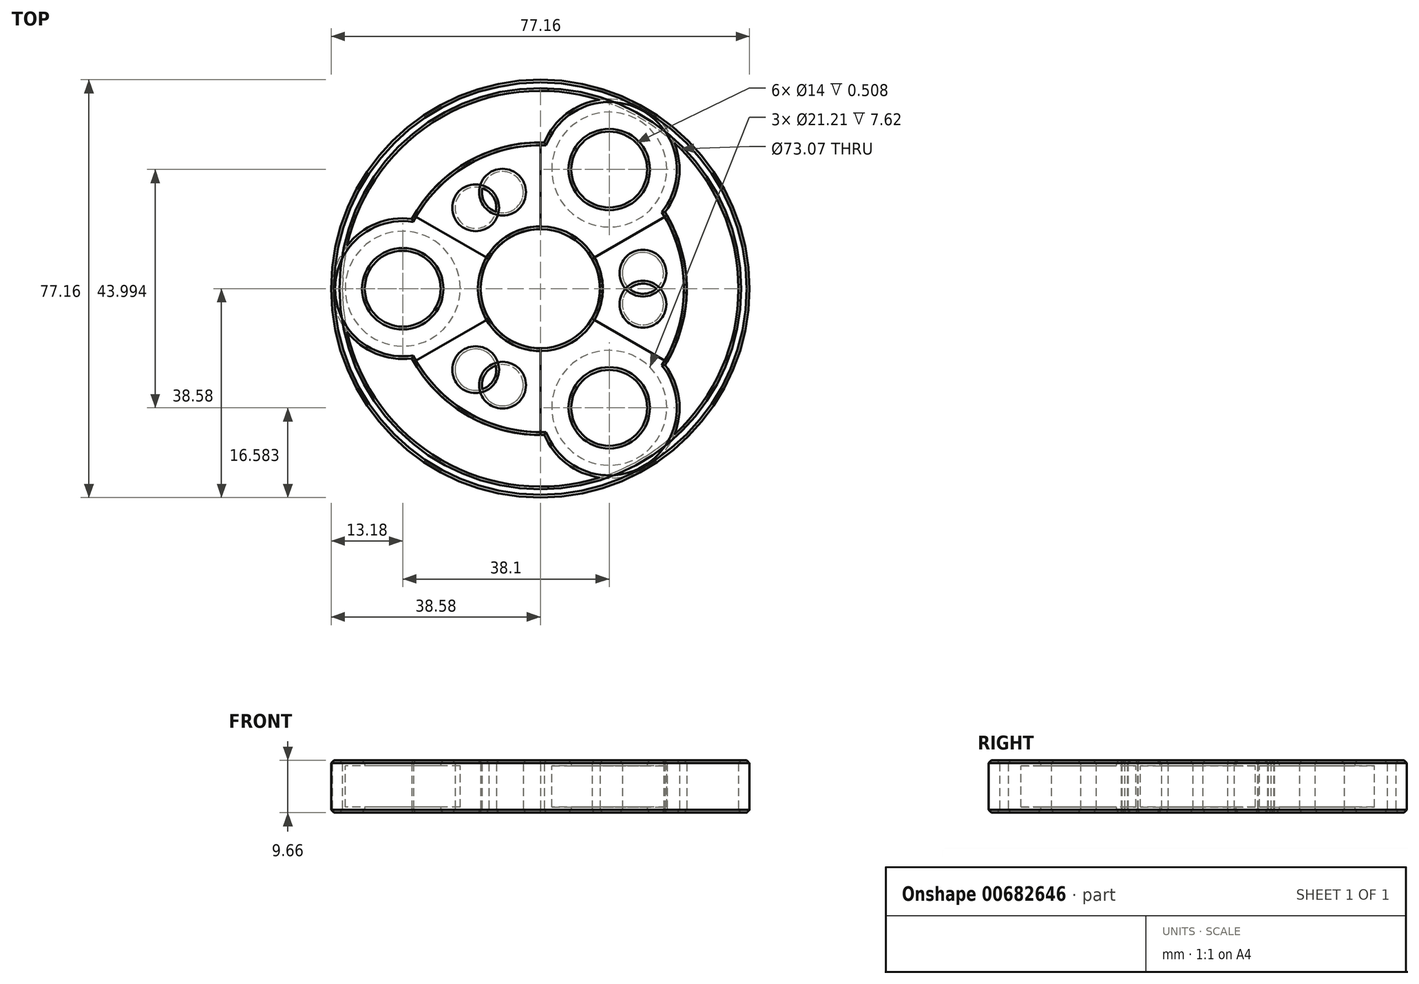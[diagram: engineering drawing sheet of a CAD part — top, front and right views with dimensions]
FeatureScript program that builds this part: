
annotation { "Feature Type Name" : "Feature", "Feature Type Description" : "" }
export const myFeature = defineFeature(function(context is Context, id is Id, definition is map)
    precondition{}
    {
        {
            var Q0;
            Q0=qCreatedBy(makeId("Top.planeOp"),FACE);
            var sketch = newSketch(context, id + "F0", { "sketchPlane" : qUnion([Q0])});
            skArc(sketch, "E0", {"start": v(0, 11) * mm, "mid": v(-11, 0) * mm, "end": v(0, -11) * mm});
            skCircle(sketch, "E1", {"center": v(-25.4, 0) * mm, "radius": 7 * mm});
            skLineSegment(sketch, "E2", {"start": v(0, 15.12) * mm, "end": v(0, 11) * mm});
            skLineSegment(sketch, "E3.trimOffspring", {"start": v(0, -11) * mm, "end": v(0, -15.12) * mm});
            skArc(sketch, "E4", {"start": v(0, 27) * mm, "mid": v(-13.81, 23.2) * mm, "end": v(-23.74, 12.87) * mm});
            skLineSegment(sketch, "E5", {"start": v(0, -27) * mm, "end": v(0, -24.4) * mm});
            skArc(sketch, "E6.trimOffspring", {"start": v(-23.74, -12.87) * mm, "mid": v(-13.81, -23.2) * mm, "end": v(0, -27) * mm});
            skArc(sketch, "E7.trimOffspring", {"start": v(-23.74, 12.87) * mm, "mid": v(-38.38, 0) * mm, "end": v(-23.74, -12.87) * mm});
            skLineSegment(sketch, "E8.trimOffspring", {"start": v(0, 24.4) * mm, "end": v(0, 27) * mm});
            skLineSegment(sketch, "E9.trimOffspring", {"start": v(0, 11) * mm, "end": v(0, 15.12) * mm});
            skLineSegment(sketch, "E10.trimOffspring", {"start": v(0, -15.12) * mm, "end": v(0, -11) * mm});
            skLineSegment(sketch, "E11", {"start": v(0, -27) * mm, "end": v(0, -11) * mm});
            skLineSegment(sketch, "E12.trimOffspring", {"start": v(0, 11) * mm, "end": v(0, 27) * mm});
            skCircle(sketch, "E13", {"center": v(-11.94, -14.95) * mm, "radius": 3.81 * mm});
            skCircle(sketch, "E14", {"center": v(-11.94, 14.95) * mm, "radius": 3.81 * mm});
            skSolve(sketch);
        }
        {
            var Q0;
            Q0=makeQuery(id+"F0.imprint","IMPRINT",FACE,{"disambiguationData":[TD([[makeQuery(id+"F0.imprint","IMPRINT",EDGE,{"derivedFrom":sQuery(id+"F0.wireOp",EDGE,"E1")}),-1.0]])]});
            var Q1;
            Q1=makeQuery(id+"F0.imprint","IMPRINT",FACE,{"disambiguationData":[TD([[makeQuery(id+"F0.imprint","IMPRINT",EDGE,{"derivedFrom":sQuery(id+"F0.wireOp",EDGE,"E0")}),-1.0]])]});
            extrude(context, id + "F1", {"entities" : qUnion([Q0, Q1]), "endBound" : BoundingType.SYMMETRIC, "depth" : 9.65 * mm, "offsetDistance" : 25.4 * mm});
        }
        {
            var Q0;
            Q0=qCreatedBy(makeId("Top.planeOp"),FACE);
            var sketch = newSketch(context, id + "F2", { "sketchPlane" : qUnion([Q0])});
            skCircle(sketch, "E15", {"center": v(-25.4, 0) * mm, "radius": 10.6 * mm});
            skSolve(sketch);
        }
        {
            var Q0;
            Q0=makeQuery(id+"F2.imprint","IMPRINT",FACE,{"disambiguationData":[TD([[makeQuery(id+"F2.imprint","IMPRINT",EDGE,{"derivedFrom":sQuery(id+"F2.wireOp",EDGE,"E15")}),1.0]])]});
            extrude(context, id + "F3", {"entities" : qUnion([Q0]), "operationType" : NewBodyOperationType.REMOVE, "endBound" : BoundingType.SYMMETRIC, "oppositeDirection" : true, "depth" : 7.62 * mm, "offsetDistance" : 25.4 * mm});
        }
        {
            var Q0;
            Q0=makeQuery(id+"F1.opExtrude","CAP_EDGE",EDGE,{"disambiguationData":[OSD([sQuery(id+"F0.wireOp",EDGE,"FDxAq660-G2Gj-sM5A-0gwt-84sQ9BPtuJKZ")])],"isStart":false});
            var Q1;
            Q1=makeQuery(id+"F1.opExtrude","CAP_EDGE",EDGE,{"disambiguationData":[OSD([sQuery(id+"F0.wireOp",EDGE,"c339bfc4-3b5d-439c-90ae-d1dc327cff93.trimOffspring")])],"isStart":false});
            var Q2;
            Q2=makeQuery(id+"F1.opExtrude","CAP_EDGE",EDGE,{"disambiguationData":[OSD([sQuery(id+"F0.wireOp",EDGE,"FDxAq660-G2Gj-sM5A-0gwt-84sQ9BPtuJKZ")])],"isStart":true});
            var Q3;
            Q3=makeQuery(id+"F1.opExtrude","CAP_EDGE",EDGE,{"disambiguationData":[OSD([sQuery(id+"F0.wireOp",EDGE,"c339bfc4-3b5d-439c-90ae-d1dc327cff93.trimOffspring")])],"isStart":true});
            var Q4;
            Q4=makeQuery(id+"F1.opExtrude","CAP_EDGE",EDGE,{"disambiguationData":[OSD([sQuery(id+"F0.wireOp",EDGE,"3xJli1Q5-KWSZ-uJhN-Jffc-vn0jT8D6R8OS")])],"isStart":true});
            var Q5;
            Q5=makeQuery(id+"F1.opExtrude","CAP_EDGE",EDGE,{"disambiguationData":[OSD([sQuery(id+"F0.wireOp",EDGE,"3xJli1Q5-KWSZ-uJhN-Jffc-vn0jT8D6R8OS")])],"isStart":false});
            var Q6;
            Q6=makeQuery(id+"F1.opExtrude","CAP_EDGE",EDGE,{"disambiguationData":[OSD([sQuery(id+"F0.wireOp",EDGE,"E0")])],"isStart":true});
            var Q7;
            Q7=makeQuery(id+"F1.opExtrude","CAP_EDGE",EDGE,{"disambiguationData":[OSD([sQuery(id+"F0.wireOp",EDGE,"E0")])],"isStart":false});
            var Q8;
            Q8=makeQuery(id+"F1.opExtrude","CAP_EDGE",EDGE,{"disambiguationData":[OSD([sQuery(id+"F0.wireOp",EDGE,"E1")])],"isStart":true});
            var Q9;
            Q9=makeQuery(id+"F1.opExtrude","CAP_EDGE",EDGE,{"disambiguationData":[OSD([sQuery(id+"F0.wireOp",EDGE,"E1")])],"isStart":false});
            var Q10;
            Q10=makeQuery(id+"F1.opExtrude","CAP_EDGE",EDGE,{"disambiguationData":[OSD([sQuery(id+"F0.wireOp",EDGE,"E4")])],"isStart":true});
            var Q11;
            Q11=makeQuery(id+"F1.opExtrude","CAP_EDGE",EDGE,{"disambiguationData":[OSD([sQuery(id+"F0.wireOp",EDGE,"E4")])],"isStart":false});
            var Q12;
            Q12=makeQuery(id+"F1.opExtrude","CAP_EDGE",EDGE,{"disambiguationData":[OSD([sQuery(id+"F0.wireOp",EDGE,"E7.trimOffspring")])],"isStart":false});
            var Q13;
            Q13=makeQuery(id+"F1.opExtrude","CAP_EDGE",EDGE,{"disambiguationData":[OSD([sQuery(id+"F0.wireOp",EDGE,"E6.trimOffspring")])],"isStart":false});
            var Q14;
            Q14=makeQuery(id+"F1.opExtrude","CAP_EDGE",EDGE,{"disambiguationData":[OSD([sQuery(id+"F0.wireOp",EDGE,"E7.trimOffspring")])],"isStart":true});
            var Q15;
            Q15=makeQuery(id+"F1.opExtrude","CAP_EDGE",EDGE,{"disambiguationData":[OSD([sQuery(id+"F0.wireOp",EDGE,"E6.trimOffspring")])],"isStart":true});
            var Q16;
            Q16=makeQuery(id+"F1.opExtrude","CAP_EDGE",EDGE,{"disambiguationData":[OSD([sQuery(id+"F0.wireOp",EDGE,"E13")])],"isStart":true});
            var Q17;
            Q17=makeQuery(id+"F1.opExtrude","CAP_EDGE",EDGE,{"disambiguationData":[OSD([sQuery(id+"F0.wireOp",EDGE,"E14")])],"isStart":true});
            var Q18;
            Q18=makeQuery(id+"F1.opExtrude","CAP_EDGE",EDGE,{"disambiguationData":[OSD([sQuery(id+"F0.wireOp",EDGE,"E13")])],"isStart":false});
            var Q19;
            Q19=makeQuery(id+"F1.opExtrude","CAP_EDGE",EDGE,{"disambiguationData":[OSD([sQuery(id+"F0.wireOp",EDGE,"E14")])],"isStart":false});
            chamfer(context, id + "F4", {"entities" : qUnion([Q0, Q1, Q2, Q3, Q4, Q5, Q6, Q7, Q8, Q9, Q10, Q11, Q12, Q13, Q14, Q15, Q16, Q17, Q18, Q19]), "width" : 0.5 * mm, "tangentPropagation" : true});
        }
        {
            var Q0;
            Q0=qCreatedBy(makeId("Top.planeOp"),FACE);
            var sketch = newSketch(context, id + "F5", { "sketchPlane" : qUnion([Q0])});
            skCircle(sketch, "E16", {"center": v(0, 0) * mm, "radius": 38.58 * mm});
            skCircle(sketch, "E17", {"center": v(0, 0) * mm, "radius": 36.53 * mm});
            skSolve(sketch);
        }
        {
            var Q0;
            Q0=makeQuery(id+"F5.imprint","IMPRINT",FACE,{"disambiguationData":[TD([[makeQuery(id+"F5.imprint","IMPRINT",EDGE,{"derivedFrom":sQuery(id+"F5.wireOp",EDGE,"E16")}),1.0]])]});
            extrude(context, id + "F6", {"entities" : qUnion([Q0]), "endBound" : BoundingType.SYMMETRIC, "depth" : 9.65 * mm, "offsetDistance" : 25.4 * mm});
        }
        {
            var Q0;
            Q0=makeQuery(id+"F1.opExtrude","SWEPT_BODY",BODY,{"disambiguationData":[OSD([sQuery(id+"F0.wireOp",EDGE,"E0"),sQuery(id+"F0.wireOp",EDGE,"3xJli1Q5-KWSZ-uJhN-Jffc-vn0jT8D6R8OS"),sQuery(id+"F0.wireOp",EDGE,"E1"),sQuery(id+"F0.wireOp",EDGE,"FDxAq660-G2Gj-sM5A-0gwt-84sQ9BPtuJKZ"),sQuery(id+"F0.wireOp",EDGE,"E2"),sQuery(id+"F0.wireOp",EDGE,"c339bfc4-3b5d-439c-90ae-d1dc327cff93.trimOffspring"),sQuery(id+"F0.wireOp",EDGE,"E3.trimOffspring")])]});
            var Q1;
            Q1=makeQuery(id+"F1.opExtrude","SWEPT_FACE",FACE,{"disambiguationData":[OSD([sQuery(id+"F0.wireOp",EDGE,"E0")])]});
            circularPattern(context, id + "F7", {"entities" : qUnion([Q0]), "axis" : qUnion([Q1]), "angle" : 360 * degree, "instanceCount" : 3, "equalSpace" : true});
        }
        {
            var Q0;
            Q0=makeQuery(id+"F6.opExtrude","CAP_EDGE",EDGE,{"disambiguationData":[OSD([sQuery(id+"F5.wireOp",EDGE,"E16")])],"isStart":false});
            var Q1;
            Q1=makeQuery(id+"F6.opExtrude","CAP_EDGE",EDGE,{"disambiguationData":[OSD([sQuery(id+"F5.wireOp",EDGE,"E17")])],"isStart":false});
            var Q2;
            Q2=makeQuery(id+"F6.opExtrude","CAP_EDGE",EDGE,{"disambiguationData":[OSD([sQuery(id+"F5.wireOp",EDGE,"E16")])],"isStart":true});
            var Q3;
            Q3=makeQuery(id+"F6.opExtrude","CAP_EDGE",EDGE,{"disambiguationData":[OSD([sQuery(id+"F5.wireOp",EDGE,"E17")])],"isStart":true});
            chamfer(context, id + "F8", {"entities" : qUnion([Q0, Q1, Q2, Q3]), "width" : 0.5 * mm, "tangentPropagation" : true});
        }
    });
